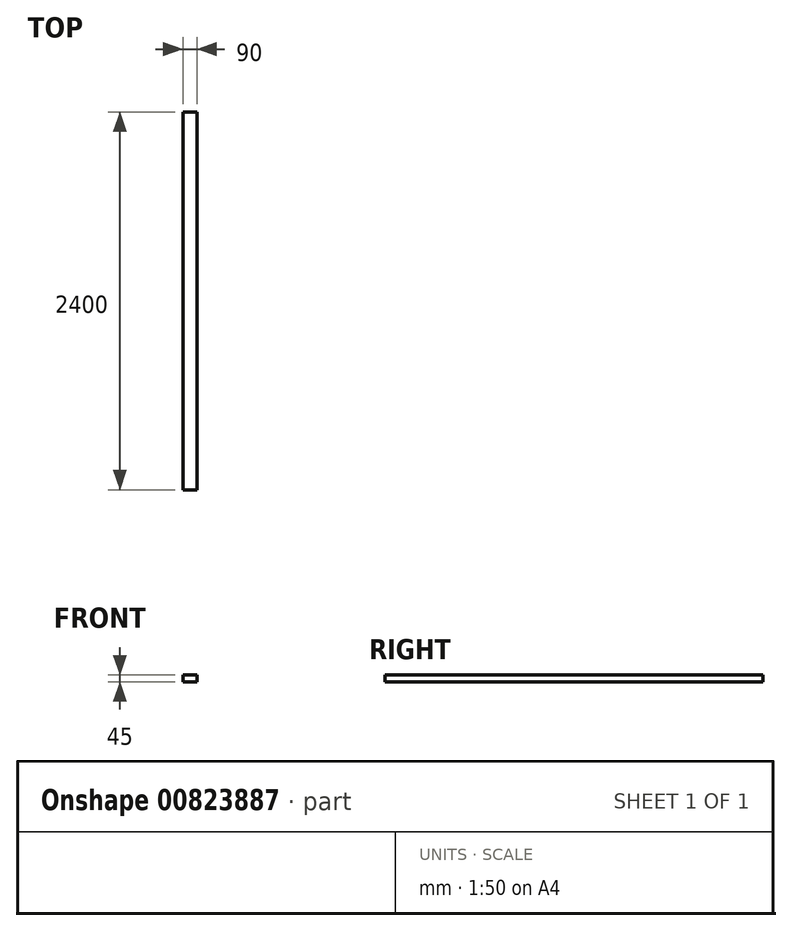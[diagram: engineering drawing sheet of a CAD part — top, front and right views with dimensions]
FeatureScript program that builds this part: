
annotation { "Feature Type Name" : "Feature", "Feature Type Description" : "" }
export const myFeature = defineFeature(function(context is Context, id is Id, definition is map)
    precondition{}
    {
        {
            var Q0;
            Q0=qCreatedBy(makeId("Front.planeOp"),FACE);
            var sketch = newSketch(context, id + "F0", { "sketchPlane" : qUnion([Q0])});
            skLineSegment(sketch, "E0.bottom", {"start": v(-45, 22.5) * mm, "end": v(45, 22.5) * mm});
            skLineSegment(sketch, "E0.top", {"start": v(-45, -22.5) * mm, "end": v(45, -22.5) * mm});
            skLineSegment(sketch, "E0.left", {"start": v(-45, 22.5) * mm, "end": v(-45, -22.5) * mm});
            skLineSegment(sketch, "E0.right", {"start": v(45, 22.5) * mm, "end": v(45, -22.5) * mm});
            skPoint(sketch, "E0.middle", {"position": v(0, 0) * mm});
            skSolve(sketch);
        }
        {
            var Q0;
            Q0=makeQuery(id+"F0.imprint","IMPRINT",FACE,{"disambiguationData":[TD([[makeQuery(id+"F0.imprint","IMPRINT",EDGE,{"derivedFrom":sQuery(id+"F0.wireOp",EDGE,"E0.bottom")}),-1.0]])]});
            extrude(context, id + "F1", {"entities" : qUnion([Q0]), "endBound" : BoundingType.SYMMETRIC, "depth" : 2400 * mm, "offsetDistance" : 25 * mm});
        }
    });
